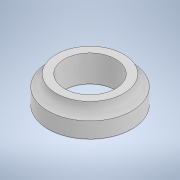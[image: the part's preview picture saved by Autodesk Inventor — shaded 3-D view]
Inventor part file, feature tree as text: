
AUTODESK INVENTOR PART (.ipt)
format: ipt  version: 2021 (Build 250183000, 183)  size: 143,360 bytes
history: native  units: in
note: dims shown in document units (in); Inventor stores cm internally (conversion verified against a paired STEP export)
features: revolve x1, fillet x1, sketch x1
ambient origin geometry x8: Origin, YZ Plane, XZ Plane, XY Plane, X Axis, Y Axis, Z Axis, Center Point
bodies: Solid1 (feature_tree)
feature tree (3):
  revolve  "Revolution1"  [1 undecoded]
  fillet  "Fillet1"  Radius=0.4331in
  sketch  "Sketch1"  dims[d0=0.7087in d1=0.4724in d2=0.4331in d3=0.0591in d4=0.1969in d5=90.0deg d6=0.0197in]
note: 1 required parameter value undecoded (feature->parameter linkage not recoverable at this tier; creation-order binding heuristic only, values carry confidence <= 0.55)
